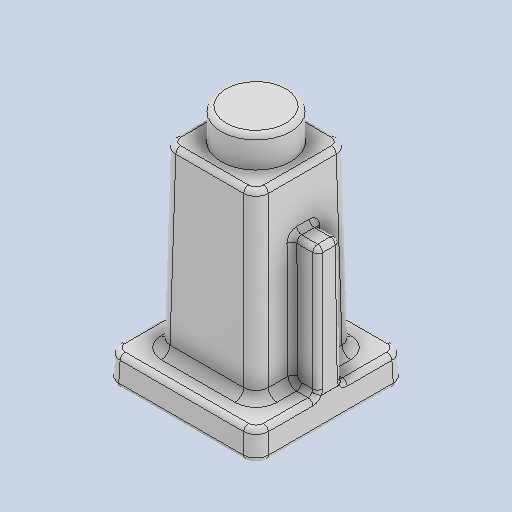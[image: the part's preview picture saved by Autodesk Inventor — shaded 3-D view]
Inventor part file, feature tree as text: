
AUTODESK INVENTOR PART (.ipt)
format: ipt  version: 2024.2 (Build 282272000, 272)  size: 274,944 bytes
history: native  units: in
note: dims shown in document units (in); Inventor stores cm internally (conversion verified against a paired STEP export)
features: fillet x1
ambient origin geometry x8: Origin, YZ Plane, XZ Plane, XY Plane, X Axis, Y Axis, Z Axis, Center Point
bodies: Solid1 (feature_tree)
feature tree (1):
  fillet  "Fillet5"  [1 undecoded]
note: 1 required parameter value undecoded (feature->parameter linkage not recoverable at this tier; creation-order binding heuristic only, values carry confidence <= 0.55)
